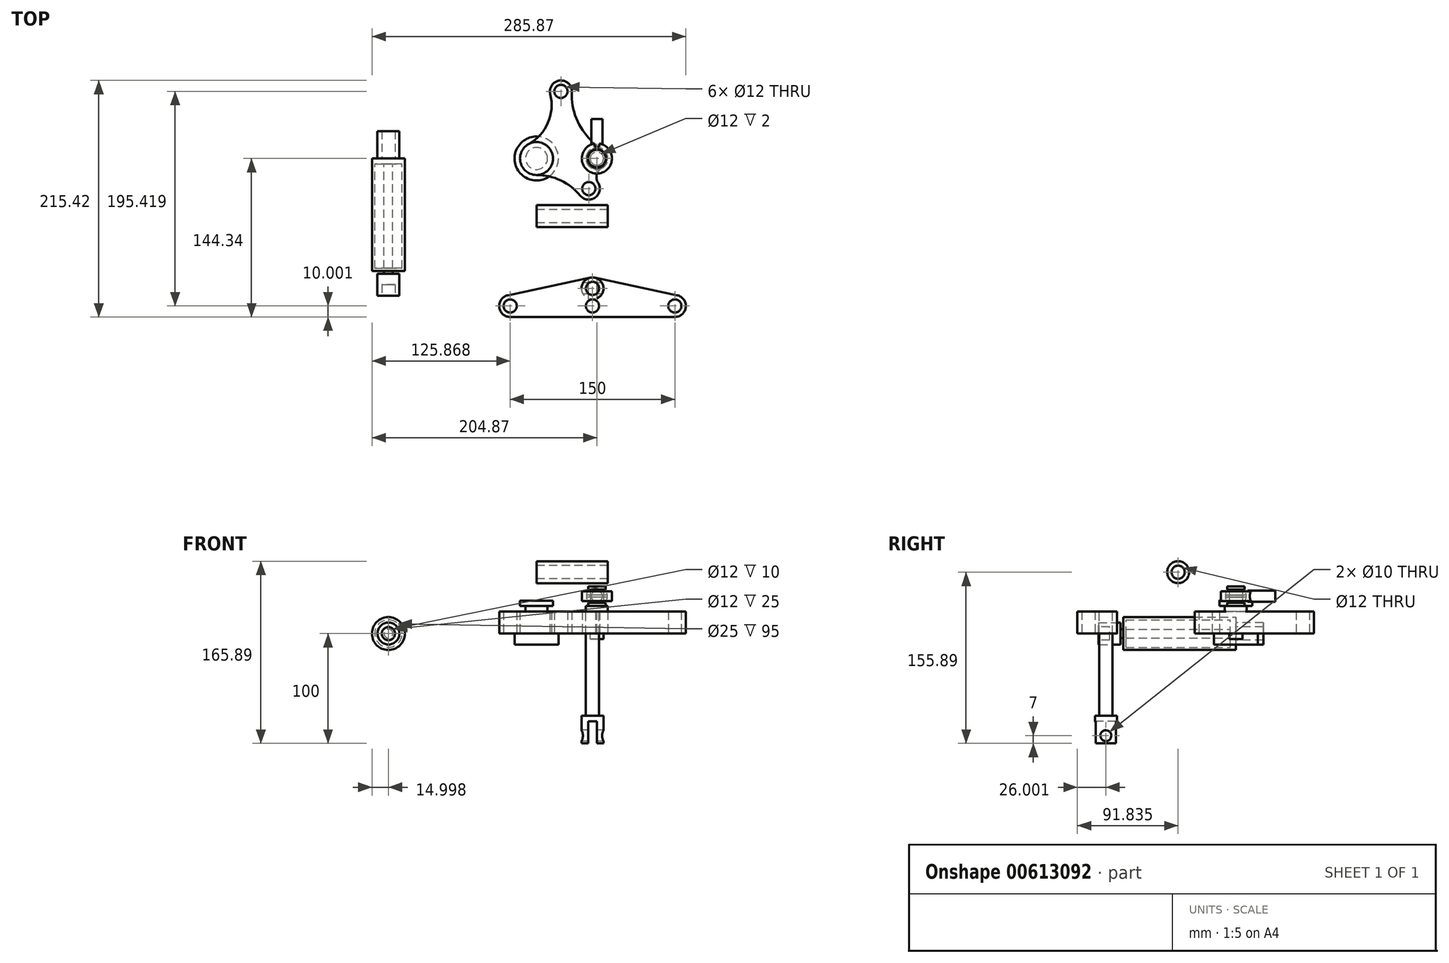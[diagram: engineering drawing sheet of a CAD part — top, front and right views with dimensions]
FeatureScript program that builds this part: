
annotation { "Feature Type Name" : "Feature", "Feature Type Description" : "" }
export const myFeature = defineFeature(function(context is Context, id is Id, definition is map)
    precondition{}
    {
        {
            var Q0;
            Q0=qCreatedBy(makeId("Top.planeOp"),FACE);
            var sketch = newSketch(context, id + "F0", { "sketchPlane" : qUnion([Q0])});
            skCircle(sketch, "E0", {"center": v(0, 0) * mm, "radius": 10 * mm});
            skCircle(sketch, "E1", {"center": v(55, 0) * mm, "radius": 6 * mm});
            skCircle(sketch, "E2", {"center": v(22.23, 61.08) * mm, "radius": 6 * mm});
            skCircle(sketch, "E3", {"center": v(22.23, 61.08) * mm, "radius": 10 * mm});
            skCircle(sketch, "E4", {"center": v(0, 0) * mm, "radius": 15 * mm});
            skCircle(sketch, "E5", {"center": v(55, 0) * mm, "radius": 10 * mm});
            skLineSegment(sketch, "E6", {"start": v(22.23, 61.08) * mm, "end": v(0, 0) * mm, "construction": true});
            skLineSegment(sketch, "E7", {"start": v(0, 0) * mm, "end": v(55, 0) * mm, "construction": true});
            skCircle(sketch, "E8", {"center": v(47.63, -27.5) * mm, "radius": 6 * mm});
            skCircle(sketch, "E9", {"center": v(47.63, -27.5) * mm, "radius": 10 * mm});
            skLineSegment(sketch, "E10", {"start": v(0, 0) * mm, "end": v(47.63, -27.5) * mm, "construction": true});
            skArc(sketch, "E11", {"start": v(-7.24, 13.14) * mm, "mid": v(10.4, 32.52) * mm, "end": v(12.54, 58.63) * mm});
            skArc(sketch, "E12", {"start": v(32.22, 60.57) * mm, "mid": v(38.92, 30.7) * mm, "end": v(60.1, 8.6) * mm});
            skArc(sketch, "E13", {"start": v(39.9, -33.85) * mm, "mid": v(22.07, -19.95) * mm, "end": v(0, -15) * mm});
            skArc(sketch, "E14", {"start": v(59.56, -8.9) * mm, "mid": v(54.87, -14.7) * mm, "end": v(56.03, -22.07) * mm});
            skSolve(sketch);
        }
        {
            var Q0;
            Q0=qSketchRegion(id+"F0",true);
            extrude(context, id + "F1", {"entities" : qUnion([Q0]), "depth" : 20 * mm});
        }
        {
            var Q0;
            Q0=makeQuery(id+"F1.opExtrude","CAP_FACE",FACE,{"disambiguationData":[OSD([sQuery(id+"F0.wireOp",EDGE,"E0"),sQuery(id+"F0.wireOp",EDGE,"E1"),sQuery(id+"F0.wireOp",EDGE,"E2"),sQuery(id+"F0.wireOp",EDGE,"E3"),sQuery(id+"F0.wireOp",EDGE,"E4"),sQuery(id+"F0.wireOp",EDGE,"E5"),sQuery(id+"F0.wireOp",EDGE,"7eYs1WeX-2swm-OC1l-bZu6-TTdB08adliAf"),sQuery(id+"F0.wireOp",EDGE,"nQsTL9GD-XLsh-tJj3-fAuQ-5O212QxCRfNk"),sQuery(id+"F0.wireOp",EDGE,"hc34mphg-32rM-w2y4-HKMr-pzHpQo0iNHix")])],"isStart":true});
            var sketch = newSketch(context, id + "F2", { "sketchPlane" : qUnion([Q0])});
            skCircle(sketch, "E15", {"center": v(0, 0) * mm, "radius": 20 * mm});
            skSolve(sketch);
        }
        {
            var Q0;
            Q0=qSketchRegion(id+"F2",true);
            extrude(context, id + "F3", {"entities" : qUnion([Q0]), "depth" : 10 * mm});
        }
        {
            var Q0;
            Q0=makeQuery(id+"F3.opExtrude","CAP_FACE",FACE,{"disambiguationData":[OSD([sQuery(id+"F2.wireOp",EDGE,"E15")])],"isStart":true});
            var sketch = newSketch(context, id + "F4", { "sketchPlane" : qUnion([Q0])});
            skCircle(sketch, "E16", {"center": v(0, 0) * mm, "radius": 10 * mm});
            skSolve(sketch);
        }
        {
            var Q0;
            Q0=qSketchRegion(id+"F4",true);
            extrude(context, id + "F5", {"entities" : qUnion([Q0]), "operationType" : NewBodyOperationType.ADD, "depth" : 25 * mm});
        }
        {
            var Q0;
            Q0=makeQuery(id+"F5.opExtrude","CAP_FACE",FACE,{"disambiguationData":[OSD([sQuery(id+"F4.wireOp",EDGE,"E16")])],"isStart":false});
            var sketch = newSketch(context, id + "F6", { "sketchPlane" : qUnion([Q0])});
            skCircle(sketch, "E17", {"center": v(0, 0) * mm, "radius": 15 * mm});
            skSolve(sketch);
        }
        {
            var Q0;
            Q0=qSketchRegion(id+"F6",true);
            extrude(context, id + "F7", {"entities" : qUnion([Q0]), "operationType" : NewBodyOperationType.ADD, "depth" : 5 * mm});
        }
        {
            var Q0;
            Q0=makeQuery(id+"F1.opExtrude","CAP_FACE",FACE,{"disambiguationData":[OSD([sQuery(id+"F0.wireOp",EDGE,"E0"),sQuery(id+"F0.wireOp",EDGE,"E1"),sQuery(id+"F0.wireOp",EDGE,"E2"),sQuery(id+"F0.wireOp",EDGE,"E3"),sQuery(id+"F0.wireOp",EDGE,"E4"),sQuery(id+"F0.wireOp",EDGE,"E5"),sQuery(id+"F0.wireOp",EDGE,"7eYs1WeX-2swm-OC1l-bZu6-TTdB08adliAf"),sQuery(id+"F0.wireOp",EDGE,"nQsTL9GD-XLsh-tJj3-fAuQ-5O212QxCRfNk"),sQuery(id+"F0.wireOp",EDGE,"hc34mphg-32rM-w2y4-HKMr-pzHpQo0iNHix")])],"isStart":false});
            var sketch = newSketch(context, id + "F8", { "sketchPlane" : qUnion([Q0])});
            skCircle(sketch, "E18", {"center": v(55, 0) * mm, "radius": 10 * mm});
            skSolve(sketch);
        }
        {
            var Q0;
            Q0=qSketchRegion(id+"F8",true);
            extrude(context, id + "F9", {"entities" : qUnion([Q0]), "depth" : 5 * mm});
        }
        {
            var Q0;
            Q0=makeQuery(id+"F9.opExtrude","CAP_FACE",FACE,{"disambiguationData":[OSD([sQuery(id+"F8.wireOp",EDGE,"E18")])],"isStart":false});
            var sketch = newSketch(context, id + "F10", { "sketchPlane" : qUnion([Q0])});
            skCircle(sketch, "E19", {"center": v(55, 0) * mm, "radius": 8 * mm});
            skSolve(sketch);
        }
        {
            var Q0;
            Q0=qSketchRegion(id+"F10",true);
            extrude(context, id + "F11", {"entities" : qUnion([Q0]), "operationType" : NewBodyOperationType.ADD, "depth" : 3 * mm});
        }
        {
            var Q0;
            Q0=makeQuery(id+"F11.opExtrude","CAP_FACE",FACE,{"disambiguationData":[OSD([sQuery(id+"F10.wireOp",EDGE,"E19")])],"isStart":false});
            var sketch = newSketch(context, id + "F12", { "sketchPlane" : qUnion([Q0])});
            skCircle(sketch, "E20", {"center": v(55, 0) * mm, "radius": 6 * mm});
            skSolve(sketch);
        }
        {
            var Q0;
            Q0=qSketchRegion(id+"F12",true);
            extrude(context, id + "F13", {"entities" : qUnion([Q0]), "operationType" : NewBodyOperationType.ADD, "depth" : 12 * mm});
        }
        {
            var Q0;
            Q0=makeQuery(id+"F13.opExtrude","CAP_FACE",FACE,{"disambiguationData":[OSD([sQuery(id+"F12.wireOp",EDGE,"E20")])],"isStart":false});
            var sketch = newSketch(context, id + "F14", { "sketchPlane" : qUnion([Q0])});
            skCircle(sketch, "E21", {"center": v(55, 0) * mm, "radius": 8 * mm});
            skSolve(sketch);
        }
        {
            var Q0;
            Q0=qSketchRegion(id+"F14",true);
            extrude(context, id + "F15", {"entities" : qUnion([Q0]), "operationType" : NewBodyOperationType.ADD, "depth" : 3 * mm});
        }
        {
            var Q0;
            Q0=makeQuery(id+"F9.opExtrude","CAP_FACE",FACE,{"disambiguationData":[OSD([sQuery(id+"F8.wireOp",EDGE,"E18")])],"isStart":true});
            var sketch = newSketch(context, id + "F16", { "sketchPlane" : qUnion([Q0])});
            skCircle(sketch, "E22", {"center": v(55, 0) * mm, "radius": 6 * mm});
            skSolve(sketch);
        }
        {
            var Q0;
            Q0=qSketchRegion(id+"F16",true);
            extrude(context, id + "F17", {"entities" : qUnion([Q0]), "operationType" : NewBodyOperationType.ADD, "depth" : 25 * mm});
        }
        {
            var Q0;
            Q0=qCreatedBy(makeId("Front.planeOp"),FACE);
            var sketch = newSketch(context, id + "F18", { "sketchPlane" : qUnion([Q0])});
            skLineSegment(sketch, "E23.0", {"start": v(47, 28) * mm, "end": v(63, 28) * mm, "construction": true});
            skLineSegment(sketch, "E24.0", {"start": v(47, 40) * mm, "end": v(63, 40) * mm, "construction": true});
            skLineSegment(sketch, "E25", {"start": v(55, 46.06) * mm, "end": v(55, 21.94) * mm, "construction": true});
            skPoint(sketch, "E25.startSnap0", {"position": v(55, 40) * mm});
            skLineSegment(sketch, "E26", {"start": v(76.42, 34) * mm, "end": v(32.2, 34) * mm, "construction": true});
            skPoint(sketch, "E26.startSnap0", {"position": v(55, 34) * mm});
            skLineSegment(sketch, "E27", {"start": v(61, 35) * mm, "end": v(61, 33) * mm, "construction": true});
            skLineSegment(sketch, "E28", {"start": v(61, 35) * mm, "end": v(64.48, 35) * mm});
            skLineSegment(sketch, "E29", {"start": v(61, 33) * mm, "end": v(64.48, 33) * mm});
            skLineSegment(sketch, "E30", {"start": v(61, 33) * mm, "end": v(61, 35) * mm});
            skArc(sketch, "E31", {"start": v(64.48, 35) * mm, "mid": v(64.53, 34) * mm, "end": v(64.48, 33) * mm});
            skSolve(sketch);
        }
        {
            var Q0;
            Q0=qSketchRegion(id+"F18",true);
            var Q1;
            Q1=sQuery(id+"F18.wireOp",EDGE,"E25");
            revolve(context, id + "F19", {"entities" : qUnion([Q0]), "axis" : qUnion([Q1]), "revolveType" : RevolveType.FULL});
        }
        {
            var Q0;
            Q0=qCreatedBy(makeId("Front.planeOp"),FACE);
            var sketch = newSketch(context, id + "F20", { "sketchPlane" : qUnion([Q0])});
            skArc(sketch, "E32", {"start": v(48.78, 41.22) * mm, "mid": v(55, 24.47) * mm, "end": v(61.22, 41.22) * mm, "construction": true});
            skLineSegment(sketch, "E33.0", {"start": v(45.52, 33) * mm, "end": v(64.48, 33) * mm, "construction": true});
            skLineSegment(sketch, "E34.0", {"start": v(45.52, 35) * mm, "end": v(64.48, 35) * mm, "construction": true});
            skLineSegment(sketch, "E35", {"start": v(63.4, 38.5) * mm, "end": v(68.73, 38.5) * mm});
            skLineSegment(sketch, "E36", {"start": v(68.73, 38.5) * mm, "end": v(68.73, 29.5) * mm});
            skLineSegment(sketch, "E37", {"start": v(68.73, 29.5) * mm, "end": v(63.4, 29.5) * mm});
            skLineSegment(sketch, "E38", {"start": v(87.4, 34) * mm, "end": v(34.56, 34) * mm, "construction": true});
            skArc(sketch, "E39", {"start": v(63.4, 38.5) * mm, "mid": v(64.53, 34) * mm, "end": v(63.4, 29.5) * mm});
            skLineSegment(sketch, "E40", {"start": v(55, 53.1) * mm, "end": v(55, 13.25) * mm, "construction": true});
            skSolve(sketch);
        }
        {
            var Q0;
            Q0=qSketchRegion(id+"F20",true);
            var Q1;
            Q1=sQuery(id+"F20.wireOp",EDGE,"E40");
            revolve(context, id + "F21", {"entities" : qUnion([Q0]), "axis" : qUnion([Q1]), "revolveType" : RevolveType.FULL});
        }
        {
            var Q0;
            Q0=qCreatedBy(makeId("Front.planeOp"),FACE);
            cPlane(context, id + "F22", {"entities" : qUnion([Q0]), "cplaneType" : CPlaneType.OFFSET, "offset" : 11 * mm, "oppositeDirection" : true, "width" : 150 * mm, "height" : 150 * mm});
        }
        {
            var Q0;
            Q0=qCreatedBy(id+"F22.planeOp",FACE);
            var sketch = newSketch(context, id + "F23", { "sketchPlane" : qUnion([Q0])});
            skLineSegment(sketch, "E41.0", {"start": v(41.27, 38.5) * mm, "end": v(68.73, 38.5) * mm, "construction": true});
            skLineSegment(sketch, "E42.0", {"start": v(41.27, 29.5) * mm, "end": v(68.73, 29.5) * mm, "construction": true});
            skLineSegment(sketch, "E43", {"start": v(68.73, 43.55) * mm, "end": v(68.73, 34.45) * mm, "construction": true});
            skLineSegment(sketch, "E44", {"start": v(41.27, 34.45) * mm, "end": v(41.27, 43.55) * mm, "construction": true});
            skLineSegment(sketch, "E45", {"start": v(55, 56.1) * mm, "end": v(55, 16.33) * mm, "construction": true});
            skLineSegment(sketch, "E46", {"start": v(74.02, 34) * mm, "end": v(35.67, 34) * mm, "construction": true});
            skCircle(sketch, "E47", {"center": v(55, 34) * mm, "radius": 5 * mm});
            skSolve(sketch);
        }
        {
            var Q0;
            Q0=qSketchRegion(id+"F23",true);
            extrude(context, id + "F24", {"entities" : qUnion([Q0]), "operationType" : NewBodyOperationType.ADD, "oppositeDirection" : true, "depth" : 25 * mm});
        }
        {
            var Q0;
            Q0=qCreatedBy(makeId("Front.planeOp"),FACE);
            var sketch = newSketch(context, id + "F25", { "sketchPlane" : qUnion([Q0])});
            skCircle(sketch, "E48", {"center": v(-134.87, 0) * mm, "radius": 15 * mm});
            skSolve(sketch);
        }
        {
            var Q0;
            Q0=qSketchRegion(id+"F25",true);
            extrude(context, id + "F26", {"entities" : qUnion([Q0]), "depth" : 100 * mm});
        }
        {
            var Q0;
            Q0=makeQuery(id+"F26.opExtrude","CAP_FACE",FACE,{"disambiguationData":[OSD([sQuery(id+"F25.wireOp",EDGE,"E48")])],"isStart":false});
            shell(context, id + "F27", {"entities" : qUnion([Q0]), "thickness" : 2.5 * mm});
        }
        {
            var Q0;
            Q0=makeQuery(id+"F26.opExtrude","CAP_FACE",FACE,{"disambiguationData":[OSD([sQuery(id+"F25.wireOp",EDGE,"E48")])],"isStart":false});
            cPlane(context, id + "F28", {"entities" : qUnion([Q0]), "cplaneType" : CPlaneType.OFFSET, "offset" : 100 * mm, "oppositeDirection" : true, "width" : 150 * mm, "height" : 150 * mm});
        }
        {
            var Q0;
            Q0=qCreatedBy(id+"F28.planeOp",FACE);
            var sketch = newSketch(context, id + "F29", { "sketchPlane" : qUnion([Q0])});
            skCircle(sketch, "E49", {"center": v(-134.87, 0) * mm, "radius": 12.5 * mm});
            skSolve(sketch);
        }
        {
            var Q0;
            Q0=qSketchRegion(id+"F29",true);
            extrude(context, id + "F30", {"entities" : qUnion([Q0]), "depth" : 5 * mm});
        }
        {
            var Q0;
            Q0=makeQuery(id+"F30.opExtrude","CAP_FACE",FACE,{"disambiguationData":[OSD([sQuery(id+"F29.wireOp",EDGE,"E49")])],"isStart":false});
            var sketch = newSketch(context, id + "F31", { "sketchPlane" : qUnion([Q0])});
            skCircle(sketch, "E50", {"center": v(-134.87, 0) * mm, "radius": 4 * mm});
            skSolve(sketch);
        }
        {
            var Q0;
            Q0=qSketchRegion(id+"F31",true);
            extrude(context, id + "F32", {"entities" : qUnion([Q0]), "operationType" : NewBodyOperationType.ADD, "depth" : 100 * mm});
        }
        {
            var Q0;
            Q0=makeQuery(id+"F26.opExtrude","CAP_FACE",FACE,{"disambiguationData":[OSD([sQuery(id+"F25.wireOp",EDGE,"E48")])],"isStart":false});
            var sketch = newSketch(context, id + "F33", { "sketchPlane" : qUnion([Q0])});
            skCircle(sketch, "E51", {"center": v(-134.87, 0) * mm, "radius": 15 * mm});
            skCircle(sketch, "E52", {"center": v(-134.87, 0) * mm, "radius": 4 * mm});
            skSolve(sketch);
        }
        {
            var Q0;
            Q0=qSketchRegion(id+"F33",true);
            extrude(context, id + "F34", {"entities" : qUnion([Q0]), "operationType" : NewBodyOperationType.ADD, "depth" : 2.5 * mm});
        }
        {
            var Q0;
            Q0=makeQuery(id+"F32.opExtrude","CAP_FACE",FACE,{"disambiguationData":[OSD([sQuery(id+"F31.wireOp",EDGE,"E50")])],"isStart":false});
            var sketch = newSketch(context, id + "F35", { "sketchPlane" : qUnion([Q0])});
            skCircle(sketch, "E53", {"center": v(-134.87, 0) * mm, "radius": 10 * mm});
            skSolve(sketch);
        }
        {
            var Q0;
            Q0=qSketchRegion(id+"F35",true);
            extrude(context, id + "F36", {"entities" : qUnion([Q0]), "operationType" : NewBodyOperationType.ADD, "depth" : 20 * mm});
        }
        {
            var Q0;
            Q0=makeQuery(id+"F26.opExtrude","CAP_FACE",FACE,{"disambiguationData":[OSD([sQuery(id+"F25.wireOp",EDGE,"E48")])],"isStart":true});
            var sketch = newSketch(context, id + "F37", { "sketchPlane" : qUnion([Q0])});
            skCircle(sketch, "E54", {"center": v(134.87, 0) * mm, "radius": 10 * mm});
            skCircle(sketch, "E55", {"center": v(134.87, 0) * mm, "radius": 6 * mm});
            skSolve(sketch);
        }
        {
            var Q0;
            Q0=qCreatedBy(makeId("Top.planeOp"),FACE);
            var sketch = newSketch(context, id + "F38", { "sketchPlane" : qUnion([Q0])});
            skCircle(sketch, "E56", {"center": v(51, -134.34) * mm, "radius": 6 * mm});
            skCircle(sketch, "E57", {"center": v(126, -134.34) * mm, "radius": 6 * mm});
            skCircle(sketch, "E58", {"center": v(-24, -134.34) * mm, "radius": 6 * mm});
            skLineSegment(sketch, "E59", {"start": v(51, -58.71) * mm, "end": v(51, -260.51) * mm, "construction": true});
            skLineSegment(sketch, "E60", {"start": v(-69.62, -134.34) * mm, "end": v(303.46, -134.34) * mm, "construction": true});
            skLineSegment(sketch, "E61", {"start": v(303.46, -134.34) * mm, "end": v(303.46, -135.94) * mm, "construction": true});
            skCircle(sketch, "E62", {"center": v(-24, -134.34) * mm, "radius": 10 * mm});
            skCircle(sketch, "E63", {"center": v(126, -134.34) * mm, "radius": 10 * mm});
            skCircle(sketch, "E64", {"center": v(51, -134.34) * mm, "radius": 10 * mm});
            skLineSegment(sketch, "E65", {"start": v(48.91, -108.56) * mm, "end": v(-26.09, -124.56) * mm});
            skLineSegment(sketch, "E66", {"start": v(-24, -144.34) * mm, "end": v(51, -144.34) * mm});
            skLineSegment(sketch, "E67", {"start": v(51, -144.34) * mm, "end": v(126, -144.34) * mm});
            skLineSegment(sketch, "E68", {"start": v(128.08, -124.56) * mm, "end": v(53.08, -108.56) * mm});
            skCircle(sketch, "E69", {"center": v(51, -118.34) * mm, "radius": 6 * mm});
            skCircle(sketch, "E70", {"center": v(51, -118.34) * mm, "radius": 10 * mm});
            skSolve(sketch);
        }
        {
            var Q0;
            Q0=qSketchRegion(id+"F38",true);
            var Q1;
            {var subQ0=sQuery(id+"F38.wireOp",EDGE,"E64");var subQ1=makeQuery(id+"F38.imprint","INTERSECT",VERTEX,{"derivedFrom":[subQ0,sQuery(id+"F38.wireOp",EDGE,"E69")]});Q1=makeQuery(id+"F38.imprint","IMPRINT",FACE,{"disambiguationData":[TD([[makeQuery(id+"F38.imprint","IMPRINT",EDGE,{"disambiguationData":[TD([[subQ1,1.0]])],"derivedFrom":subQ0}),1.0]])]});}
            extrude(context, id + "F39", {"entities" : qUnion([Q0, Q1]), "depth" : 20 * mm});
        }
        {
            var Q0;
            Q0=makeQuery(id+"F39.opExtrude","CAP_FACE",FACE,{"disambiguationData":[OSD([sQuery(id+"F38.wireOp",EDGE,"E56"),sQuery(id+"F38.wireOp",EDGE,"E57"),sQuery(id+"F38.wireOp",EDGE,"E58"),sQuery(id+"F38.wireOp",EDGE,"E62"),sQuery(id+"F38.wireOp",EDGE,"E63"),sQuery(id+"F38.wireOp",EDGE,"E64"),sQuery(id+"F38.wireOp",EDGE,"E65"),sQuery(id+"F38.wireOp",EDGE,"E66"),sQuery(id+"F38.wireOp",EDGE,"E67"),sQuery(id+"F38.wireOp",EDGE,"E68"),sQuery(id+"F38.wireOp",EDGE,"E69"),sQuery(id+"F38.wireOp",EDGE,"E70")])],"isStart":true});
            var sketch = newSketch(context, id + "F40", { "sketchPlane" : qUnion([Q0])});
            skCircle(sketch, "E71", {"center": v(51, 118.34) * mm, "radius": 6 * mm});
            skSolve(sketch);
        }
        {
            var Q0;
            Q0=qSketchRegion(id+"F40",true);
            var Q1;
            Q1=makeQuery(id+"F39.opExtrude","CAP_FACE",FACE,{"disambiguationData":[OSD([sQuery(id+"F38.wireOp",EDGE,"E56"),sQuery(id+"F38.wireOp",EDGE,"E57"),sQuery(id+"F38.wireOp",EDGE,"E58"),sQuery(id+"F38.wireOp",EDGE,"E62"),sQuery(id+"F38.wireOp",EDGE,"E63"),sQuery(id+"F38.wireOp",EDGE,"E64"),sQuery(id+"F38.wireOp",EDGE,"E65"),sQuery(id+"F38.wireOp",EDGE,"E66"),sQuery(id+"F38.wireOp",EDGE,"E67"),sQuery(id+"F38.wireOp",EDGE,"E68"),sQuery(id+"F38.wireOp",EDGE,"E69"),sQuery(id+"F38.wireOp",EDGE,"E70")])],"isStart":false});
            extrude(context, id + "F41", {"entities" : qUnion([Q0]), "depth" : 75 * mm, "hasSecondDirection" : true, "secondDirectionBound" : SecondDirectionBoundingType.UP_TO_SURFACE, "secondDirectionOppositeDirection" : true, "secondDirectionBoundEntityFace" : qUnion([Q1]), "secondDirectionDepth" : 25 * mm});
        }
        {
            var Q0;
            Q0=makeQuery(id+"F41.opExtrude","CAP_FACE",FACE,{"disambiguationData":[OSD([sQuery(id+"F40.wireOp",EDGE,"E71")])],"isStart":false});
            var sketch = newSketch(context, id + "F42", { "sketchPlane" : qUnion([Q0])});
            skCircle(sketch, "E72", {"center": v(51, 118.34) * mm, "radius": 10 * mm});
            skSolve(sketch);
        }
        {
            var Q0;
            Q0=qSketchRegion(id+"F42",true);
            extrude(context, id + "F43", {"entities" : qUnion([Q0]), "operationType" : NewBodyOperationType.ADD, "depth" : 25 * mm});
        }
        {
            var Q0;
            Q0=makeQuery(id+"F43.opExtrude","CAP_FACE",FACE,{"disambiguationData":[OSD([sQuery(id+"F42.wireOp",EDGE,"E72")])],"isStart":false});
            var sketch = newSketch(context, id + "F44", { "sketchPlane" : qUnion([Q0])});
            skLineSegment(sketch, "E73.bottom", {"start": v(47, 104.3) * mm, "end": v(55, 104.3) * mm});
            skLineSegment(sketch, "E73.top", {"start": v(47, 132.38) * mm, "end": v(55, 132.38) * mm});
            skLineSegment(sketch, "E73.left", {"start": v(47, 104.3) * mm, "end": v(47, 132.38) * mm});
            skLineSegment(sketch, "E73.right", {"start": v(55, 104.3) * mm, "end": v(55, 132.38) * mm});
            skPoint(sketch, "E73.middle", {"position": v(51, 118.34) * mm});
            skSolve(sketch);
        }
        {
            var Q0;
            Q0=qSketchRegion(id+"F44",true);
            extrude(context, id + "F45", {"entities" : qUnion([Q0]), "operationType" : NewBodyOperationType.REMOVE, "oppositeDirection" : true, "depth" : 20 * mm});
        }
        {
            var Q0;
            Q0=makeQuery(id+"F45.boolean.opBoolean","COPY",FACE,{"derivedFrom":makeQuery(id+"F45.opExtrude","SWEPT_FACE",FACE,{"disambiguationData":[OSD([sQuery(id+"F44.wireOp",EDGE,"E73.right")])]})});
            var sketch = newSketch(context, id + "F46", { "sketchPlane" : qUnion([Q0])});
            skCircle(sketch, "E74", {"center": v(118.34, -93) * mm, "radius": 5 * mm});
            skPoint(sketch, "E74.centerSnap0", {"position": v(118.34, -80) * mm});
            skSolve(sketch);
        }
        {
            var Q0;
            Q0=qSketchRegion(id+"F46",true);
            extrude(context, id + "F47", {"entities" : qUnion([Q0]), "operationType" : NewBodyOperationType.REMOVE, "endBound" : BoundingType.THROUGH_ALL, "oppositeDirection" : true, "depth" : 25 * mm, "hasSecondDirection" : true, "secondDirectionBound" : SecondDirectionBoundingType.THROUGH_ALL, "secondDirectionOppositeDirection" : false, "secondDirectionDepth" : 25 * mm});
        }
        {
            var Q0;
            Q0=makeQuery(id+"F36.opExtrude","CAP_FACE",FACE,{"disambiguationData":[OSD([sQuery(id+"F35.wireOp",EDGE,"E53")])],"isStart":false});
            var sketch = newSketch(context, id + "F48", { "sketchPlane" : qUnion([Q0])});
            skCircle(sketch, "E75", {"center": v(-134.87, 0) * mm, "radius": 6 * mm});
            skSolve(sketch);
        }
        {
            var Q0;
            Q0=qSketchRegion(id+"F48",true);
            extrude(context, id + "F49", {"entities" : qUnion([Q0]), "operationType" : NewBodyOperationType.REMOVE, "oppositeDirection" : true, "depth" : 10 * mm});
        }
        {
            var Q0;
            Q0=qSketchRegion(id+"F37",true);
            extrude(context, id + "F50", {"entities" : qUnion([Q0]), "operationType" : NewBodyOperationType.ADD, "depth" : 25 * mm});
        }
        {
            var Q0;
            Q0=qCreatedBy(makeId("Right.planeOp"),FACE);
            var sketch = newSketch(context, id + "F51", { "sketchPlane" : qUnion([Q0])});
            skCircle(sketch, "E76", {"center": v(-52.5, 55.89) * mm, "radius": 10 * mm});
            skCircle(sketch, "E77", {"center": v(-52.5, 55.89) * mm, "radius": 6 * mm});
            skSolve(sketch);
        }
        {
            var Q0;
            Q0=qSketchRegion(id+"F51",true);
            extrude(context, id + "F52", {"entities" : qUnion([Q0]), "depth" : 65 * mm});
        }
    });
